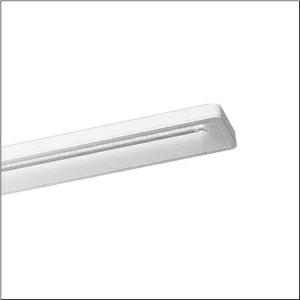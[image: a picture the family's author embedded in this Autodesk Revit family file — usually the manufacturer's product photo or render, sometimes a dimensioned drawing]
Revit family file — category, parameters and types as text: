
# Revit family: taris_r__21_5mt217703wd_caa9
name_source: partatom
category: Lighting Fixtures
units: mm (PartAtom-declared; Revit-internal decimal feet)

## family parameters
Cut with Voids When Loaded = No
Host = Face
Light Source = No
Part Type = Normal
Room Calculation Point = No
Round Connector Dimension = Use Diameter
Shared = No

## types (1)
- Taris® 21 (1 x LED, 5700 lm, 37 W, 3000K)
    Apparent Load = 37 VA
    CIE Flux Codes = 73 96 99 100 100
    Color Rendering = 80
    Color Temperature = 3000K
    Default Elevation = 1800 mm
    Description = Taris® 21, office luminaire, primary anti-glare with micro louvre, primary optical cover: axial lens, of PMMA, structured, CAT 2 (L<= 1500cd/m²), light emission: direct distribution, primary light characteristic: symmetric, installation type: surface-mounted, LED, rated luminous flux: 5.700lm, luminous efficacy: 154lm/W, light colour: 830, colour temperature: 3000K, control gear: ECG, with terminal, 5-pole, mains connection: 230V, AC, 50Hz, rated input power: 37W, housing, luminaire housing, of plastic, traffic white (RAL 9016), length: 1.510mm, width: 134mm, height: 50mm, protection rating (complete): IP20, insulation class (complete): insulation class I (protective earthing), certification: CE, ENEC, VDE, protection symbol: F, impact resistance: IK02, permissible operating ambient temperature: 0..+35°C, standard: EN 50419, packaging unit: 1 piece
    Height = 51 mm
    Lamp = 1 x LED
    Lamp Light Flux = 5700 lm
    Lamp Power = 37 W
    Lamp count = 1
    Length = 1514 mm
    Luminous efficacy = 154 lm/W
    Manufacturer = Siteco
    ModVariant = No
    Model = 5MT217703WD
    Mounting Place = Ceiling
    Mounting Type = Surface mounted
    Number of Poles = 1
    OnlyDefault = Yes
    Power Factor = 1
    Product Name = Taris® 21
    Product group = office luminaire | ceiling mounted
    ProductGroupID = 304
    Protection Class = Protection class I
    Protection Degree = IP 20
    RLX_Detail_Level = 1
    RLX_Emergency_Light_Flux = 0 lm
    RLX_Emergency_Type = 0
    RLX_Emergency_Type_DB = No
    RlxData = <blob elided: 38965 chars, md5=615627b4>
    Socket = socket
    Standby Power = 0 W
    System Light Flux = 5700 lm
    System Power = 37 W
    Type Comments = Product without accessories
    Type Image = l_1004728.jpg
    URL = http://relux.com
    VarID = ---
    Voltage = 0 V
    Weight = 0.00 kg
    Width = 134 mm

## geometry (parser evidence)
native form markers: Blend x4, Sweep x10
no freeform markers — native parametric forms only
